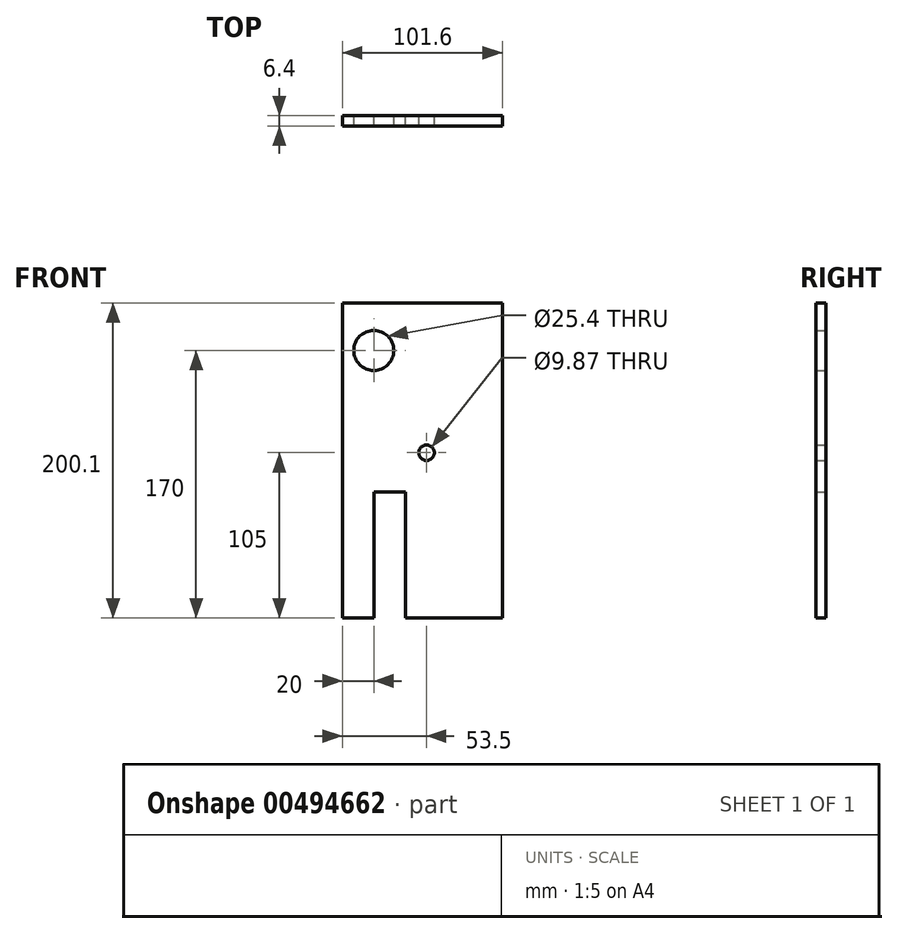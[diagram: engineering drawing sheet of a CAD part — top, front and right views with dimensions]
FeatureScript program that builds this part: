
annotation { "Feature Type Name" : "Feature", "Feature Type Description" : "" }
export const myFeature = defineFeature(function(context is Context, id is Id, definition is map)
    precondition{}
    {
        {
            var Q0;
            Q0=qCreatedBy(makeId("Front.planeOp"),FACE);
            var sketch = newSketch(context, id + "F0", { "sketchPlane" : qUnion([Q0])});
            skLineSegment(sketch, "E0.bottom", {"start": v(0, 0) * mm, "end": v(20, 0) * mm});
            skLineSegment(sketch, "E0.top", {"start": v(0, 200.1) * mm, "end": v(101.6, 200.1) * mm});
            skLineSegment(sketch, "E0.left", {"start": v(0, 0) * mm, "end": v(0, 200.1) * mm});
            skLineSegment(sketch, "E0.right", {"start": v(101.6, 0) * mm, "end": v(101.6, 200.1) * mm});
            skCircle(sketch, "E1", {"center": v(20, 170) * mm, "radius": 12.7 * mm});
            skLineSegment(sketch, "E2.top", {"start": v(20, 80) * mm, "end": v(40, 80) * mm});
            skLineSegment(sketch, "E2.left", {"start": v(20, 0) * mm, "end": v(20, 80) * mm});
            skLineSegment(sketch, "E2.right", {"start": v(40, 0) * mm, "end": v(40, 80) * mm});
            skLineSegment(sketch, "E3.trimOffspring", {"start": v(40, 0) * mm, "end": v(101.6, 0) * mm});
            skCircle(sketch, "E4", {"center": v(53.5, 105) * mm, "radius": 4.94 * mm});
            skSolve(sketch);
        }
        {
            var Q0;
            Q0 = qSketchRegion(id + "F0", true);
            extrude(context, id + "F1", {"entities" : qUnion([Q0]), "depth" : 6.4 * mm});
        }
    });
